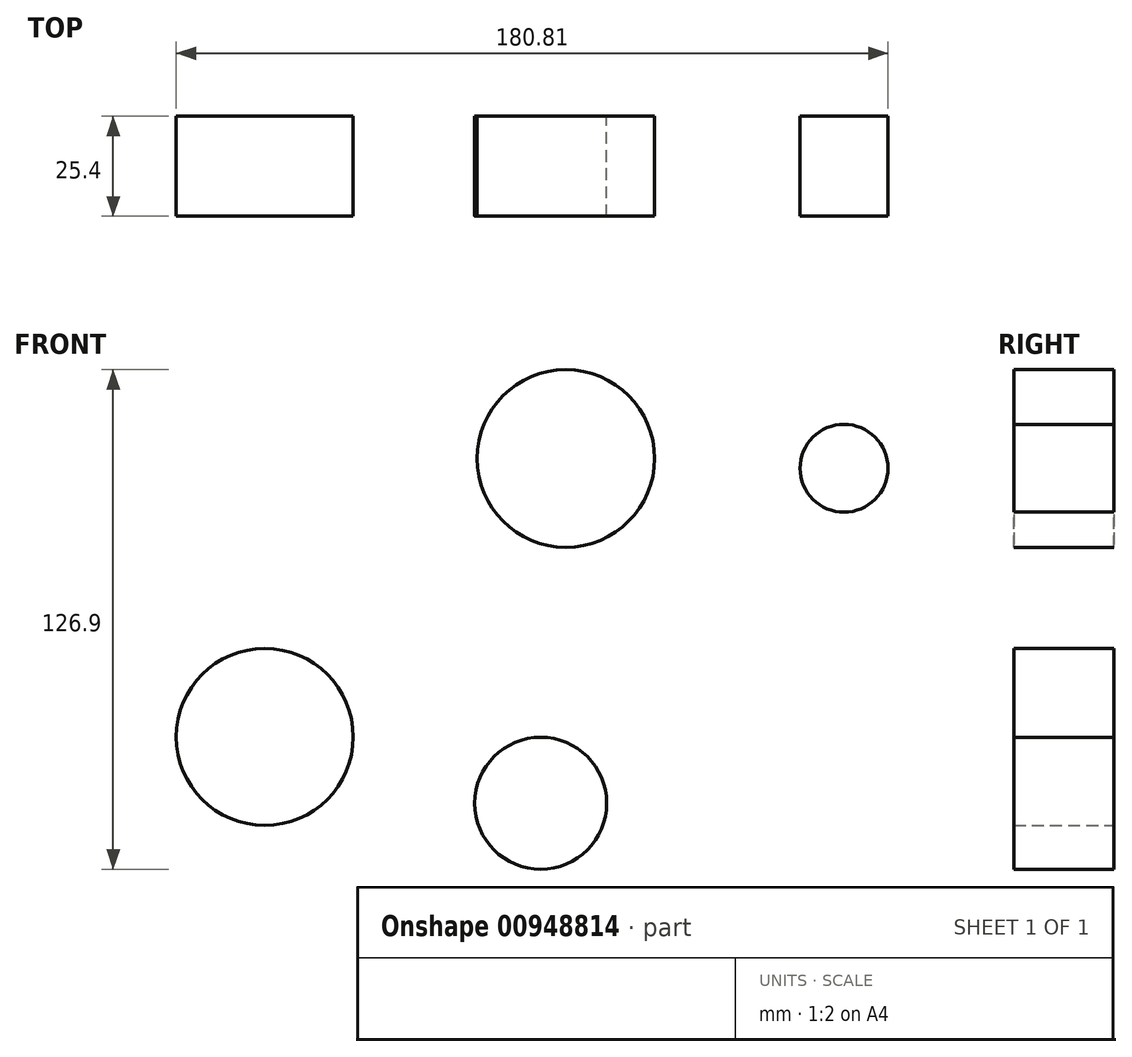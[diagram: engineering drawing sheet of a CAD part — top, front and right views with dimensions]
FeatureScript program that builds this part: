
annotation { "Feature Type Name" : "Feature", "Feature Type Description" : "" }
export const myFeature = defineFeature(function(context is Context, id is Id, definition is map)
    precondition{}
    {
        {
            var Q0;
            Q0=qCreatedBy(makeId("Front.planeOp"),FACE);
            var sketch = newSketch(context, id + "F0", { "sketchPlane" : qUnion([Q0])});
            skCircle(sketch, "E0", {"center": v(-139.78, 4.12) * mm, "radius": 22.48 * mm});
            skCircle(sketch, "E1", {"center": v(-63.3, 74.87) * mm, "radius": 22.55 * mm});
            skCircle(sketch, "E2", {"center": v(7.39, 72.38) * mm, "radius": 11.17 * mm});
            skCircle(sketch, "E3", {"center": v(-69.67, -12.73) * mm, "radius": 16.76 * mm});
            skSolve(sketch);
        }
        {
            var Q0;
            Q0 = qSketchRegion(id + "F0", true);
            extrude(context, id + "F1", {"entities" : qUnion([Q0]), "depth" : 25.4 * mm, "offsetDistance" : 25.4 * mm});
        }
    });
